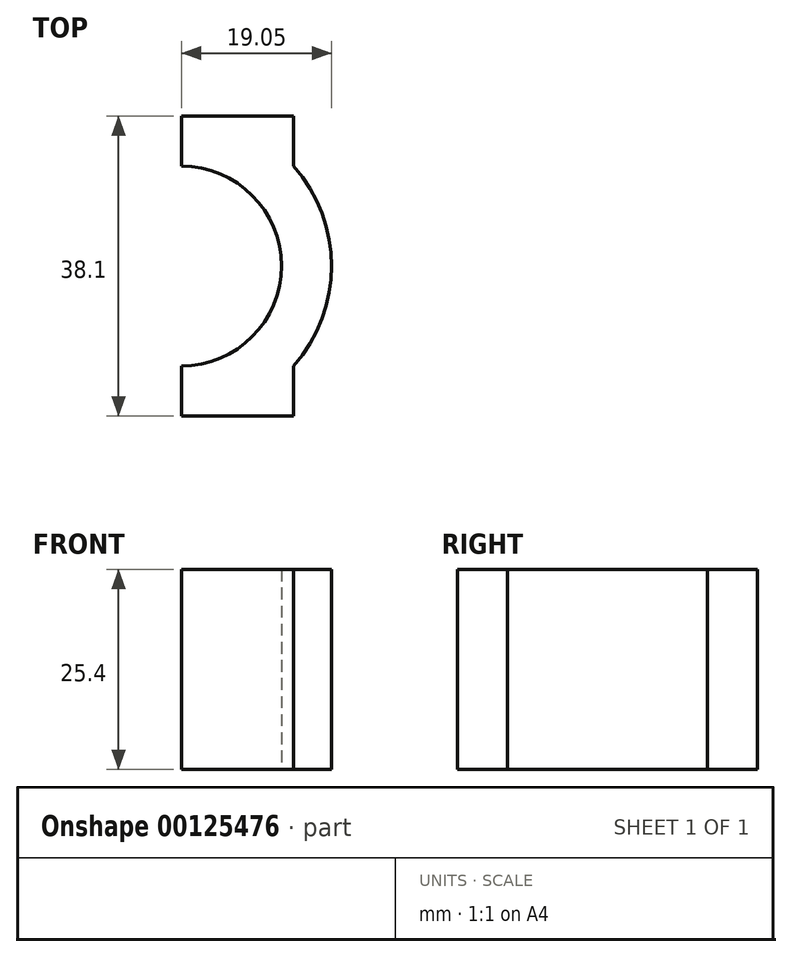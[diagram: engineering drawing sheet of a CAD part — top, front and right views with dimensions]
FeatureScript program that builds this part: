
annotation { "Feature Type Name" : "Feature", "Feature Type Description" : "" }
export const myFeature = defineFeature(function(context is Context, id is Id, definition is map)
    precondition{}
    {
        {
            var Q0;
            Q0=qCreatedBy(makeId("Top.planeOp"),FACE);
            var sketch = newSketch(context, id + "F0", { "sketchPlane" : qUnion([Q0])});
            skLineSegment(sketch, "E0.bottom", {"start": v(0, 19.05) * mm, "end": v(14.2, 19.05) * mm});
            skLineSegment(sketch, "E0.top", {"start": v(0, -19.05) * mm, "end": v(14.2, -19.05) * mm});
            skLineSegment(sketch, "E0.left", {"start": v(0, 19.05) * mm, "end": v(0, 12.7) * mm});
            skLineSegment(sketch, "E0.right", {"start": v(14.2, 19.05) * mm, "end": v(14.2, 12.7) * mm});
            skArc(sketch, "E1", {"start": v(14.2, -12.7) * mm, "mid": v(19.05, 0) * mm, "end": v(14.2, 12.7) * mm});
            skArc(sketch, "E2", {"start": v(0, -12.7) * mm, "mid": v(12.7, 0) * mm, "end": v(0, 12.7) * mm});
            skLineSegment(sketch, "E3.trimOffspring", {"start": v(0, -12.7) * mm, "end": v(0, -19.05) * mm});
            skLineSegment(sketch, "E4.trimOffspring", {"start": v(14.2, -12.7) * mm, "end": v(14.2, -19.05) * mm});
            skSolve(sketch);
        }
        {
            var Q0;
            Q0 = qSketchRegion(id + "F0", true);
            extrude(context, id + "F1", {"entities" : qUnion([Q0]), "depth" : 25.4 * mm});
        }
    });
